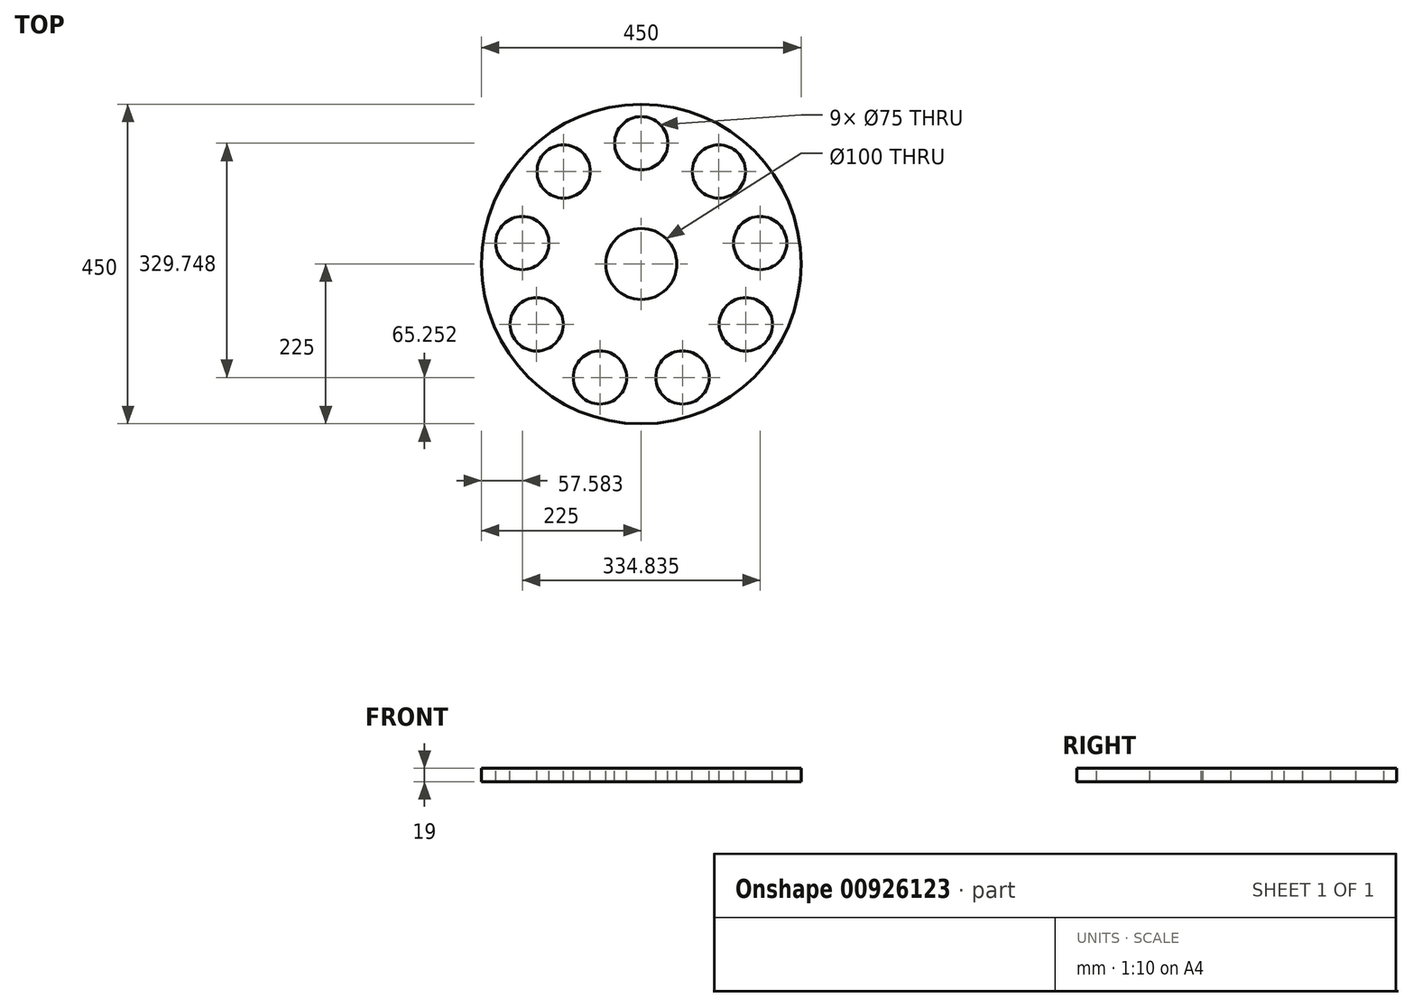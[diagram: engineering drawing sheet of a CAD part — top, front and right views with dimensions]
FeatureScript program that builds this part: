
annotation { "Feature Type Name" : "Feature", "Feature Type Description" : "" }
export const myFeature = defineFeature(function(context is Context, id is Id, definition is map)
    precondition{}
    {
        {
            var Q0;
            Q0=qCreatedBy(makeId("Top.planeOp"),FACE);
            var sketch = newSketch(context, id + "F0", { "sketchPlane" : qUnion([Q0])});
            skCircle(sketch, "E0", {"center": v(0, 0) * mm, "radius": 225 * mm});
            skSolve(sketch);
        }
        {
            var Q0;
            Q0=qSketchRegion(id+"F0",true);
            extrude(context, id + "F1", {"entities" : qUnion([Q0]), "depth" : 19 * mm, "offsetDistance" : 25 * mm});
        }
        {
            var Q0;
            Q0=makeQuery(id+"F1.opExtrude","CAP_FACE",FACE,{"disambiguationData":[OSD([sQuery(id+"F0.wireOp",EDGE,"E0")])],"isStart":false});
            var sketch = newSketch(context, id + "F2", { "sketchPlane" : qUnion([Q0])});
            skCircle(sketch, "E1", {"center": v(0, 0) * mm, "radius": 50 * mm});
            skCircle(sketch, "E2", {"center": v(0, 170) * mm, "radius": 37.5 * mm});
            skCircle(sketch, "E3.1.0", {"center": v(-109.27, 130.23) * mm, "radius": 37.5 * mm});
            skCircle(sketch, "E3.2.0", {"center": v(-167.42, 29.52) * mm, "radius": 37.5 * mm});
            skCircle(sketch, "E3.3.0", {"center": v(-147.22, -85) * mm, "radius": 37.5 * mm});
            skCircle(sketch, "E3.4.0", {"center": v(-58.14, -159.75) * mm, "radius": 37.5 * mm});
            skCircle(sketch, "E4.1.5.0", {"center": v(58.14, -159.75) * mm, "radius": 37.5 * mm});
            skCircle(sketch, "E4.1.6.0", {"center": v(147.22, -85) * mm, "radius": 37.5 * mm});
            skCircle(sketch, "E4.1.7.0", {"center": v(167.42, 29.52) * mm, "radius": 37.5 * mm});
            skCircle(sketch, "E4.1.8.0", {"center": v(109.27, 130.23) * mm, "radius": 37.5 * mm});
            skSolve(sketch);
        }
        {
            var Q0;
            Q0=qSketchRegion(id+"F2",true);
            extrude(context, id + "F3", {"entities" : qUnion([Q0]), "operationType" : NewBodyOperationType.REMOVE, "oppositeDirection" : true, "depth" : 53 * mm, "offsetDistance" : 25 * mm});
        }
    });
